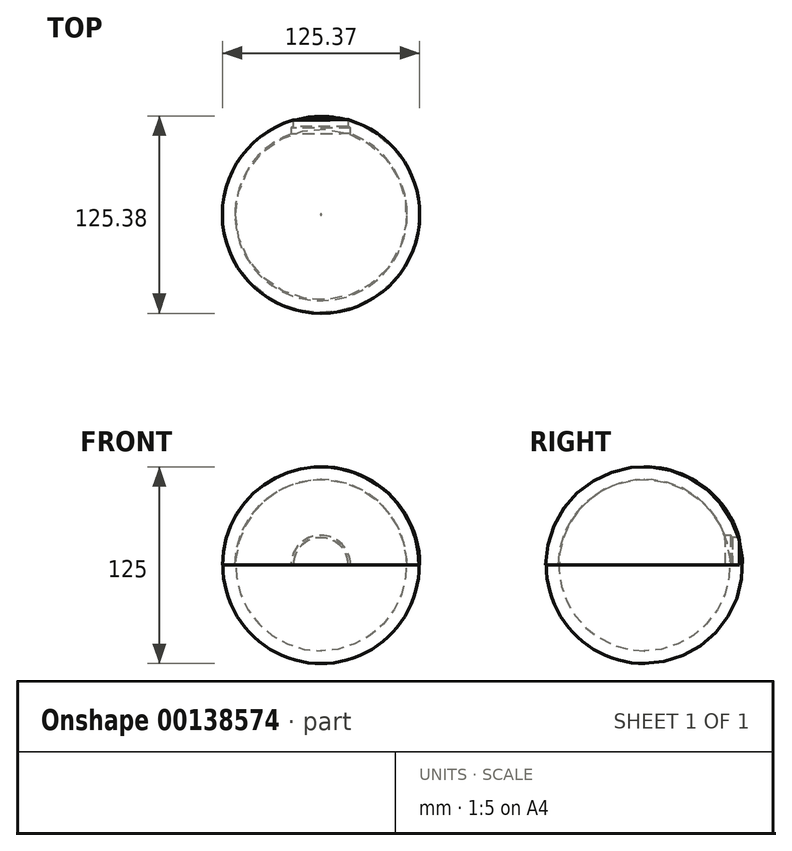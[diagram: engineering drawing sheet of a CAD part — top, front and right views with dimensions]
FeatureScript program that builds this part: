
annotation { "Feature Type Name" : "Feature", "Feature Type Description" : "" }
export const myFeature = defineFeature(function(context is Context, id is Id, definition is map)
    precondition{}
    {
        {
            var Q0;
            Q0=qCreatedBy(makeId("Front.planeOp"),FACE);
            var sketch = newSketch(context, id + "F0", { "sketchPlane" : qUnion([Q0])});
            skArc(sketch, "E0", {"start": v(62.5, 0.57) * mm, "mid": v(-0.19, 62.5) * mm, "end": v(-62.5, 0.2) * mm});
            skArc(sketch, "E1.0", {"start": v(54.5, 0.5) * mm, "mid": v(-0.16, 54.5) * mm, "end": v(-54.5, 0.18) * mm});
            skLineSegment(sketch, "E2", {"start": v(-62.5, 0.2) * mm, "end": v(-54.5, 0.18) * mm});
            skLineSegment(sketch, "E3", {"start": v(54.5, 0.5) * mm, "end": v(62.5, 0.57) * mm});
            skLineSegment(sketch, "E4", {"start": v(0.19, 62.5) * mm, "end": v(0.19, 54.5) * mm});
            skPoint(sketch, "E4.startSnap0", {"position": v(-0.19, 62.5) * mm});
            skCircle(sketch, "E5", {"center": v(0, 0) * mm, "radius": 15 * mm});
            skCircle(sketch, "E6.0", {"center": v(0, 0) * mm, "radius": 18 * mm});
            skLineSegment(sketch, "E7", {"start": v(-18, 0) * mm, "end": v(18, 0) * mm});
            skLineSegment(sketch, "E8", {"start": v(15, 0) * mm, "end": v(-15, 0) * mm});
            skSolve(sketch);
        }
        {
            var Q0;
            {var subQ0=sQuery(id+"F0.wireOp",EDGE,"E2");Q0=makeQuery(id+"F0.imprint","IMPRINT",FACE,{"disambiguationData":[TD([[makeQuery(id+"F0.imprint","IMPRINT",EDGE,{"derivedFrom":subQ0}),1.0]])]});}
            var Q1;
            Q1=sQuery(id+"F0.wireOp",EDGE,"E4");
            revolve(context, id + "F1", {"entities" : qUnion([Q0]), "axis" : qUnion([Q1]), "revolveType" : RevolveType.FULL});
        }
        {
            var Q0;
            Q0=sQuery(id+"F0.wireOp",VERTEX,"E1.0.center");
            var Q1;
            Q1=makeQuery(id+"F1.opRevolve","SWEPT_BODY",BODY,{"disambiguationData":[OSD([sQuery(id+"F0.wireOp",EDGE,"E0"),sQuery(id+"F0.wireOp",EDGE,"E1.0"),sQuery(id+"F0.wireOp",EDGE,"E2"),sQuery(id+"F0.wireOp",EDGE,"E4")])]});
            hole(context, id + "F2", {"style" : HoleStyle.SIMPLE, "endStyle" : HoleEndStyle.THROUGH, "holeDiameter" : 35 * mm, "locations" : qUnion([Q0]), "scope" : qUnion([Q1]), "isTappedThrough" : true});
        }
        {
            var Q0;
            Q0=sQuery(id+"F0.wireOp",VERTEX,"E1.0.center");
            var Q1;
            Q1=makeQuery(id+"F1.opRevolve","SWEPT_BODY",BODY,{"disambiguationData":[OSD([sQuery(id+"F0.wireOp",EDGE,"E0"),sQuery(id+"F0.wireOp",EDGE,"E1.0"),sQuery(id+"F0.wireOp",EDGE,"E2"),sQuery(id+"F0.wireOp",EDGE,"E4")])]});
            hole(context, id + "F3", {"style" : HoleStyle.SIMPLE, "endStyle" : HoleEndStyle.BLIND, "holeDiameter" : 38 * mm, "holeDepth" : 55 * mm, "locations" : qUnion([Q0]), "scope" : qUnion([Q1])});
        }
    });
